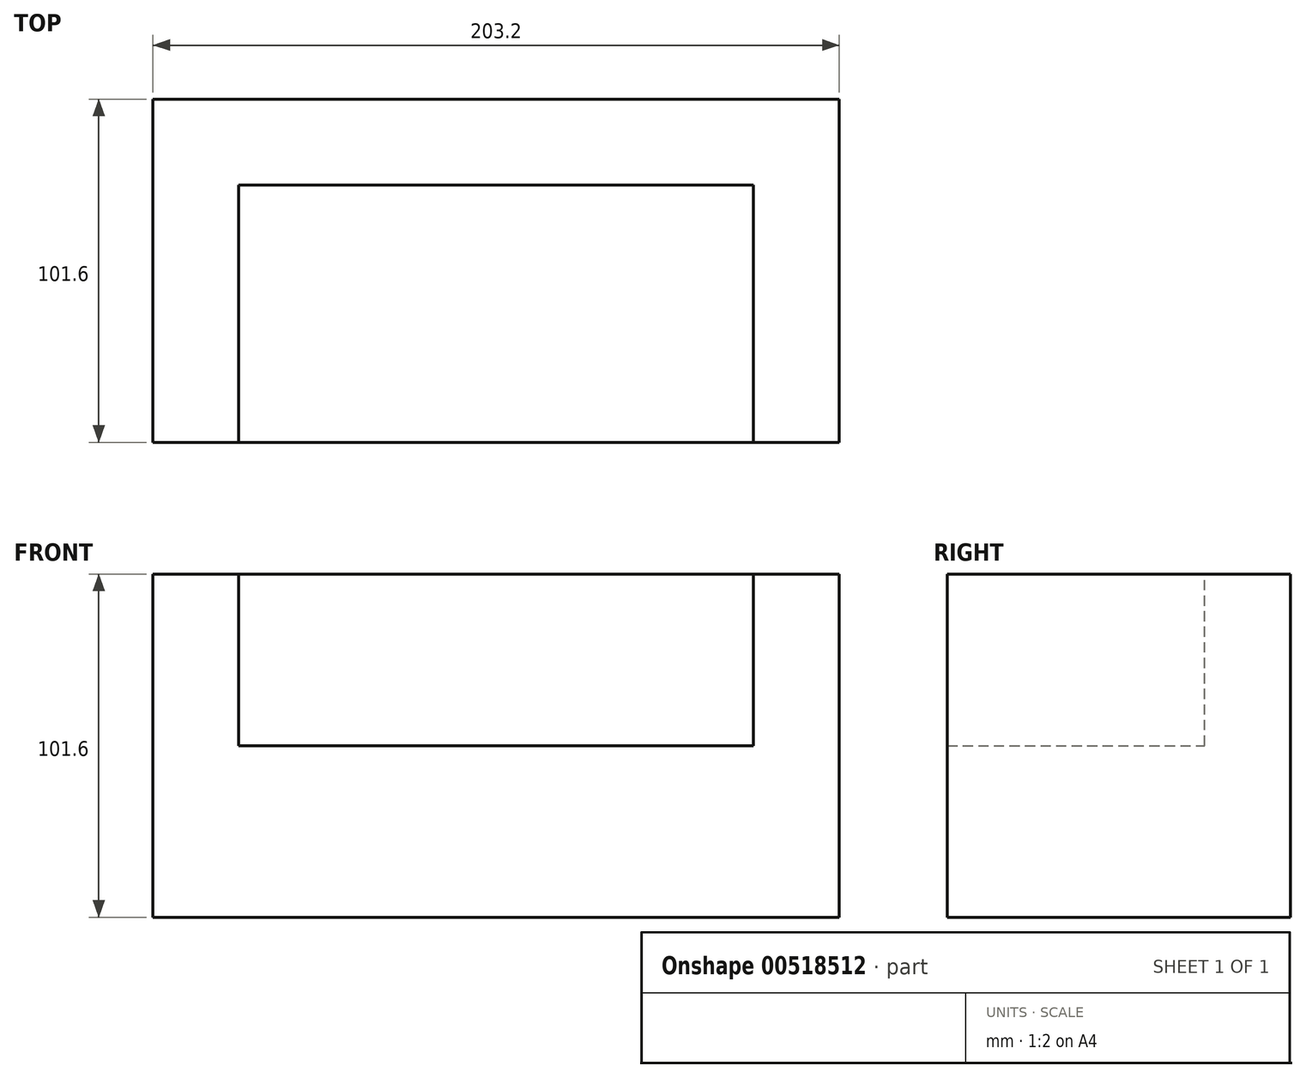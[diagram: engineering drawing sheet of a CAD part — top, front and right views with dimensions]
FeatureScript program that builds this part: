
annotation { "Feature Type Name" : "Feature", "Feature Type Description" : "" }
export const myFeature = defineFeature(function(context is Context, id is Id, definition is map)
    precondition{}
    {
        {
            var Q0;
            Q0=qCreatedBy(makeId("Front.planeOp"),FACE);
            var sketch = newSketch(context, id + "F0", { "sketchPlane" : qUnion([Q0])});
            skLineSegment(sketch, "E0.bottom", {"start": v(-128.37, 32.1) * mm, "end": v(74.83, 32.1) * mm});
            skLineSegment(sketch, "E0.top", {"start": v(-128.37, -69.5) * mm, "end": v(74.83, -69.5) * mm});
            skLineSegment(sketch, "E0.left", {"start": v(-128.37, 32.1) * mm, "end": v(-128.37, -69.5) * mm});
            skLineSegment(sketch, "E0.right", {"start": v(74.83, 32.1) * mm, "end": v(74.83, -69.5) * mm});
            skSolve(sketch);
        }
        {
            var Q0;
            Q0=qSketchRegion(id+"F0",true);
            extrude(context, id + "F1", {"entities" : qUnion([Q0]), "depth" : 101.6 * mm});
        }
        {
            var Q0;
            Q0=makeQuery(id+"F1.opExtrude","SWEPT_FACE",FACE,{"disambiguationData":[OSD([sQuery(id+"F0.wireOp",EDGE,"E0.bottom")])]});
            var sketch = newSketch(context, id + "F2", { "sketchPlane" : qUnion([Q0])});
            skLineSegment(sketch, "E1.bottom", {"start": v(-102.97, -101.6) * mm, "end": v(49.43, -101.6) * mm});
            skLineSegment(sketch, "E1.top", {"start": v(-102.97, -25.4) * mm, "end": v(49.43, -25.4) * mm});
            skLineSegment(sketch, "E1.left", {"start": v(-102.97, -101.6) * mm, "end": v(-102.97, -25.4) * mm});
            skLineSegment(sketch, "E1.right", {"start": v(49.43, -101.6) * mm, "end": v(49.43, -25.4) * mm});
            skSolve(sketch);
        }
        {
            var Q0;
            Q0=qSketchRegion(id+"F2",true);
            extrude(context, id + "F3", {"entities" : qUnion([Q0]), "operationType" : NewBodyOperationType.REMOVE, "oppositeDirection" : true, "depth" : 50.8 * mm});
        }
    });
